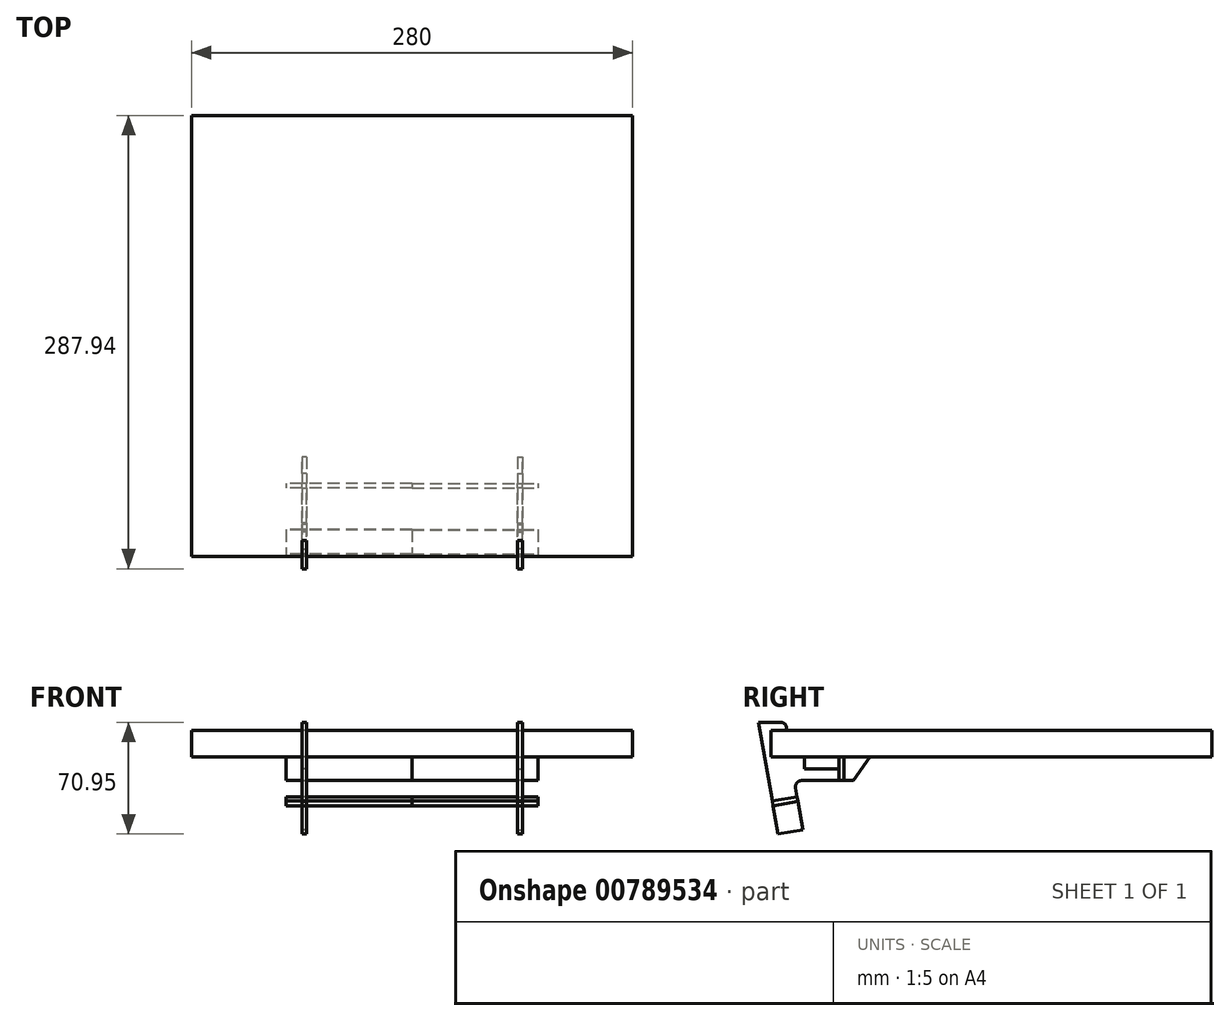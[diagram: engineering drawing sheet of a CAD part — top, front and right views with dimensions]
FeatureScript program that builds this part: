
annotation { "Feature Type Name" : "Feature", "Feature Type Description" : "" }
export const myFeature = defineFeature(function(context is Context, id is Id, definition is map)
    precondition{}
    {
        {
            var Q0;
            Q0=qCreatedBy(makeId("Top.planeOp"),FACE);
            var sketch = newSketch(context, id + "F0", { "sketchPlane" : qUnion([Q0])});
            skLineSegment(sketch, "E0.bottom", {"start": v(140, -85) * mm, "end": v(-140, -85) * mm});
            skLineSegment(sketch, "E0.top", {"start": v(140, 85) * mm, "end": v(-140, 85) * mm});
            skLineSegment(sketch, "E0.left", {"start": v(140, -85) * mm, "end": v(140, 85) * mm});
            skLineSegment(sketch, "E0.right", {"start": v(-140, -85) * mm, "end": v(-140, 85) * mm});
            skPoint(sketch, "E0.middle", {"position": v(0, 0) * mm});
            skSolve(sketch);
        }
        {
            var Q0;
            Q0=makeQuery(id+"F0.imprint","IMPRINT",FACE,{"disambiguationData":[TD([[makeQuery(id+"F0.imprint","IMPRINT",EDGE,{"derivedFrom":sQuery(id+"F0.wireOp",EDGE,"E0.bottom")}),-1.0]])]});
            extrude(context, id + "F1", {"entities" : qUnion([Q0]), "depth" : 17 * mm, "offsetDistance" : 25 * mm});
        }
        {
            var Q0;
            Q0=makeQuery(id+"F1.opExtrude","CAP_EDGE",EDGE,{"disambiguationData":[OSD([sQuery(id+"F0.wireOp",EDGE,"E0.bottom")])],"isStart":true});
            var Q1;
            Q1=qCreatedBy(makeId("Front.planeOp"),FACE);
            cPlane(context, id + "F2", {"entities" : qUnion([Q0, Q1]), "cplaneType" : CPlaneType.LINE_ANGLE, "offset" : 25 * mm, "angle" : 10 * degree, "oppositeDirection" : true, "width" : 150 * mm, "height" : 150 * mm});
        }
        {
            var Q0;
            Q0=qCreatedBy(id+"F2.planeOp",FACE);
            var sketch = newSketch(context, id + "F3", { "sketchPlane" : qUnion([Q0])});
            skLineSegment(sketch, "E1.bottom", {"start": v(70, 87.7) * mm, "end": v(67, 87.7) * mm});
            skLineSegment(sketch, "E1.top", {"start": v(70, -112.3) * mm, "end": v(67, -112.3) * mm});
            skLineSegment(sketch, "E1.left", {"start": v(70, 87.7) * mm, "end": v(70, -112.3) * mm});
            skLineSegment(sketch, "E1.right", {"start": v(67, 87.7) * mm, "end": v(67, -112.3) * mm});
            skSolve(sketch);
        }
        {
            var Q0;
            Q0=qSketchRegion(id+"F3",true);
            extrude(context, id + "F4", {"entities" : qUnion([Q0]), "oppositeDirection" : true, "depth" : 8 * mm, "offsetDistance" : 25 * mm, "hasSecondDirection" : true, "secondDirectionOppositeDirection" : false, "secondDirectionDepth" : 130 * mm});
        }
        {
            var Q0;
            Q0=makeQuery(id+"F1.opExtrude","SWEPT_BODY",BODY,{"disambiguationData":[OSD([sQuery(id+"F0.wireOp",EDGE,"E0.bottom"),sQuery(id+"F0.wireOp",EDGE,"E0.top"),sQuery(id+"F0.wireOp",EDGE,"E0.left"),sQuery(id+"F0.wireOp",EDGE,"E0.right")])]});
            var Q1;
            Q1=makeQuery(id+"F4.opExtrude","SWEPT_BODY",BODY,{"disambiguationData":[OSD([sQuery(id+"F3.wireOp",EDGE,"E1.bottom"),sQuery(id+"F3.wireOp",EDGE,"E1.top"),sQuery(id+"F3.wireOp",EDGE,"E1.left"),sQuery(id+"F3.wireOp",EDGE,"E1.right")])]});
            booleanBodies(context, id + "F5", {"operationType" : BooleanOperationType.SUBTRACTION, "tools" : qUnion([Q0]), "targets" : qUnion([Q1])});
        }
        {
            var Q0;
            Q0=makeQuery(id+"F4.opExtrude","SWEPT_FACE",FACE,{"disambiguationData":[OSD([sQuery(id+"F3.wireOp",EDGE,"E1.left")])]});
            var sketch = newSketch(context, id + "F6", { "sketchPlane" : qUnion([Q0])});
            skLineSegment(sketch, "E2.0", {"start": v(-31.06, 22) * mm, "end": v(164.2, 22) * mm});
            skLineSegment(sketch, "E3", {"start": v(62.6, -57.92) * mm, "end": v(22.04, 0) * mm});
            skLineSegment(sketch, "E4", {"start": v(22.04, 0) * mm, "end": v(90.98, -12.16) * mm, "construction": true});
            skLineSegment(sketch, "E5", {"start": v(75, 22) * mm, "end": v(75, 17) * mm});
            skLineSegment(sketch, "E6", {"start": v(84.37, -49.64) * mm, "end": v(64.67, -46.17) * mm});
            skLineSegment(sketch, "E7", {"start": v(62.6, -57.92) * mm, "end": v(64.67, -46.17) * mm});
            skPoint(sketch, "E8", {"position": v(97, 22) * mm});
            skPoint(sketch, "E9", {"position": v(19, 0) * mm});
            skSolve(sketch);
        }
        {
            var Q0;
            {var subQ0=sQuery(id+"F3.wireOp",EDGE,"E1.left");var subQ2=sQuery(id+"F3.wireOp",EDGE,"E1.bottom");var subQ3=makeQuery(id+"F4.opExtrude","SWEPT_EDGE",EDGE,{"disambiguationData":[OSD([subQ2,subQ0])]});Q0=makeQuery(id+"F6.imprint","IMPRINT",FACE,{"disambiguationData":[TD([[makeQuery(id+"F6.imprint","IMPRINT",EDGE,{"derivedFrom":subQ3}),1.0]])]});}
            var Q1;
            {var subQ0=sQuery(id+"F6.wireOp",EDGE,"E5");Q1=makeQuery(id+"F6.imprint","IMPRINT",FACE,{"disambiguationData":[TD([[makeQuery(id+"F6.imprint","IMPRINT",EDGE,{"derivedFrom":subQ0}),-1.0]])]});}
            var Q2;
            {var subQ2=sQuery(id+"F3.wireOp",EDGE,"E1.left");var subQ3=sQuery(id+"F3.wireOp",EDGE,"E1.top");var subQ8=makeQuery(id+"F4.opExtrude","SWEPT_EDGE",EDGE,{"disambiguationData":[OSD([subQ3,subQ2])]});Q2=makeQuery(id+"F6.imprint","IMPRINT",FACE,{"disambiguationData":[TD([[makeQuery(id+"F6.imprint","IMPRINT",EDGE,{"derivedFrom":subQ8}),-1.0]])]});}
            extrude(context, id + "F7", {"entities" : qUnion([Q0, Q1, Q2]), "operationType" : NewBodyOperationType.REMOVE, "oppositeDirection" : true, "depth" : 25 * mm, "offsetDistance" : 25 * mm});
        }
        {
            var Q0;
            Q0=makeQuery(id+"F4.opExtrude","SWEPT_FACE",FACE,{"disambiguationData":[OSD([sQuery(id+"F3.wireOp",EDGE,"E1.left")])]});
            var sketch = newSketch(context, id + "F8", { "sketchPlane" : qUnion([Q0])});
            skLineSegment(sketch, "E10.0", {"start": v(32.55, -15) * mm, "end": v(70.17, -15) * mm});
            skLineSegment(sketch, "E11.0", {"start": v(82.08, 52.55) * mm, "end": v(56.38, -93.2) * mm});
            skLineSegment(sketch, "E12.0", {"start": v(62.6, -57.92) * mm, "end": v(22.04, 0) * mm});
            skSolve(sketch);
        }
        {
            var Q0;
            {var subQ0=sQuery(id+"F8.wireOp",EDGE,"E10.0");Q0=makeQuery(id+"F8.imprint","IMPRINT",FACE,{"disambiguationData":[TD([[makeQuery(id+"F8.imprint","IMPRINT",EDGE,{"derivedFrom":subQ0}),-1.0]])]});}
            var Q1;
            Q1=makeQuery(id+"F4.opExtrude","SWEPT_FACE",FACE,{"disambiguationData":[OSD([sQuery(id+"F3.wireOp",EDGE,"E1.right")])]});
            extrude(context, id + "F9", {"entities" : qUnion([Q0]), "operationType" : NewBodyOperationType.REMOVE, "endBound" : BoundingType.UP_TO_SURFACE, "oppositeDirection" : true, "depth" : 25 * mm, "endBoundEntityFace" : qUnion([Q1]), "offsetDistance" : 25 * mm});
        }
        {
            var Q0;
            Q0=makeQuery(id+"F4.opExtrude","SWEPT_FACE",FACE,{"disambiguationData":[OSD([sQuery(id+"F3.wireOp",EDGE,"E1.right")])]});
            var sketch = newSketch(context, id + "F10", { "sketchPlane" : qUnion([Q0])});
            skLineSegment(sketch, "E13", {"start": v(-80.3, -49.64) * mm, "end": v(-97.67, 48.84) * mm});
            skLineSegment(sketch, "E14", {"start": v(-97.67, 48.84) * mm, "end": v(-105.31, 47.49) * mm});
            skLineSegment(sketch, "E15", {"start": v(-105.31, 47.49) * mm, "end": v(-116.05, -55.95) * mm});
            skLineSegment(sketch, "E16", {"start": v(-116.05, -55.95) * mm, "end": v(-80.3, -49.64) * mm});
            skSolve(sketch);
        }
        {
            var Q0;
            {var subQ1=sQuery(id+"F3.wireOp",EDGE,"E1.right");var subQ7=makeQuery(id+"F4.opExtrude","CAP_EDGE",EDGE,{"disambiguationData":[OSD([subQ1])],"isStart":false});Q0=makeQuery(id+"F10.imprint","IMPRINT",FACE,{"disambiguationData":[TD([[makeQuery(id+"F10.imprint","IMPRINT",EDGE,{"derivedFrom":subQ7}),1.0]])]});}
            extrude(context, id + "F11", {"entities" : qUnion([Q0]), "operationType" : NewBodyOperationType.REMOVE, "oppositeDirection" : true, "depth" : 25 * mm, "offsetDistance" : 25 * mm});
        }
        {
            var Q0;
            Q0=makeQuery(id+"F7.boolean.opBoolean","COPY",EDGE,{"derivedFrom":makeQuery(id+"F7.opExtrude","SWEPT_EDGE",EDGE,{"disambiguationData":[OSD([sQuery(id+"F6.wireOp",EDGE,"E2.0"),sQuery(id+"F6.wireOp",EDGE,"E5")])]})});
            var Q1;
            Q1=makeQuery(id+"F11.boolean.opBoolean","COPY",EDGE,{"derivedFrom":makeQuery(id+"F11.opExtrude","SWEPT_EDGE",EDGE,{"disambiguationData":[OSD([sQuery(id+"F3.wireOp",EDGE,"E1.right"),sQuery(id+"F6.wireOp",EDGE,"E2.0"),sQuery(id+"F10.wireOp",EDGE,"E13")])]})});
            var Q2;
            Q2=makeQuery(id+"F11.boolean.opBoolean","COPY",EDGE,{"derivedFrom":makeQuery(id+"F11.opExtrude","SWEPT_EDGE",EDGE,{"disambiguationData":[OSD([sQuery(id+"F3.wireOp",EDGE,"E1.right"),sQuery(id+"F6.wireOp",EDGE,"E6"),sQuery(id+"F10.wireOp",EDGE,"E13")])]})});
            var Q3;
            Q3=makeQuery(id+"F7.boolean.opBoolean","COPY",EDGE,{"derivedFrom":makeQuery(id+"F7.opExtrude","SWEPT_EDGE",EDGE,{"disambiguationData":[OSD([sQuery(id+"F6.wireOp",EDGE,"E6"),sQuery(id+"F6.wireOp",EDGE,"E7")])]})});
            var Q4;
            Q4=makeQuery(id+"F9.boolean.opBoolean","COPY",EDGE,{"derivedFrom":makeQuery(id+"F9.opExtrude","SWEPT_EDGE",EDGE,{"disambiguationData":[OSD([sQuery(id+"F8.wireOp",EDGE,"E10.0"),sQuery(id+"F8.wireOp",EDGE,"E11.0")])]})});
            var Q5;
            Q5=makeQuery(id+"F9.boolean.opBoolean","COPY",EDGE,{"derivedFrom":makeQuery(id+"F9.opExtrude","SWEPT_EDGE",EDGE,{"disambiguationData":[OSD([sQuery(id+"F8.wireOp",EDGE,"E10.0"),sQuery(id+"F8.wireOp",EDGE,"E12.0")])]})});
            var Q6;
            Q6=makeQuery(id+"F7.boolean.opBoolean","COPY",EDGE,{"derivedFrom":makeQuery(id+"F7.opExtrude","SWEPT_EDGE",EDGE,{"disambiguationData":[OSD([sQuery(id+"F0.wireOp",EDGE,"E0.bottom"),sQuery(id+"F0.wireOp",EDGE,"E0.top"),sQuery(id+"F0.wireOp",EDGE,"E0.left"),sQuery(id+"F0.wireOp",EDGE,"E0.right"),sQuery(id+"F3.wireOp",EDGE,"E1.left"),sQuery(id+"F6.wireOp",EDGE,"E3")])]})});
            fillet(context, id + "F12", {"entities" : qUnion([Q0, Q1, Q2, Q3, Q4, Q5, Q6]), "radius" : 4 * mm, "tangentPropagation" : true, "defaultsChanged" : false, "vertexSettings" : [], "allowEdgeOverflow" : false});
        }
        {
            var Q0;
            Q0=makeQuery(id+"F4.opExtrude","SWEPT_FACE",FACE,{"disambiguationData":[OSD([sQuery(id+"F3.wireOp",EDGE,"E1.right")])]});
            var sketch = newSketch(context, id + "F13", { "sketchPlane" : qUnion([Q0])});
            skLineSegment(sketch, "E17.bottom", {"start": v(-84.11, -28.06) * mm, "end": v(-83.6, -31.01) * mm});
            skLineSegment(sketch, "E17.top", {"start": v(-68.36, -25.28) * mm, "end": v(-67.84, -28.23) * mm});
            skLineSegment(sketch, "E17.left", {"start": v(-68.36, -25.28) * mm, "end": v(-84.11, -28.06) * mm});
            skLineSegment(sketch, "E17.right", {"start": v(-67.84, -28.23) * mm, "end": v(-83.6, -31.01) * mm});
            skLineSegment(sketch, "E18.bottom", {"start": v(-38.73, 0) * mm, "end": v(-41.73, 0) * mm});
            skLineSegment(sketch, "E18.top", {"start": v(-38.73, -15) * mm, "end": v(-41.73, -15) * mm});
            skLineSegment(sketch, "E18.left", {"start": v(-38.73, 0) * mm, "end": v(-38.73, -15) * mm});
            skLineSegment(sketch, "E18.right", {"start": v(-41.73, 0) * mm, "end": v(-41.73, -15) * mm});
            skLineSegment(sketch, "E19.0", {"start": v(-29.73, 0) * mm, "end": v(-85, 0) * mm});
            skLineSegment(sketch, "E20.0", {"start": v(-34.63, -15) * mm, "end": v(-65.4, -15) * mm});
            skLineSegment(sketch, "E21.0", {"start": v(-69.34, -19.7) * mm, "end": v(-65.37, -42.23) * mm});
            skLineSegment(sketch, "E22.0", {"start": v(-81.13, -45.01) * mm, "end": v(-92.11, 17.3) * mm});
            skSolve(sketch);
        }
        {
            var Q0;
            Q0=qSketchRegion(id+"F13",true);
            var Q1;
            Q1=qCreatedBy(makeId("Right.planeOp"),FACE);
            var Q2;
            Q2=makeQuery(id+"F4.opExtrude","SWEPT_FACE",FACE,{"disambiguationData":[OSD([sQuery(id+"F3.wireOp",EDGE,"E1.left")])]});
            extrude(context, id + "F14", {"entities" : qUnion([Q0]), "endBound" : BoundingType.UP_TO_SURFACE, "depth" : 25 * mm, "endBoundEntityFace" : qUnion([Q1]), "offsetDistance" : 25 * mm, "hasSecondDirection" : true, "secondDirectionBound" : BoundingType.UP_TO_SURFACE, "secondDirectionOppositeDirection" : true, "secondDirectionDepth" : 17.8 * mm, "secondDirectionBoundEntityFace" : qUnion([Q2]), "hasSecondDirectionOffset" : true, "secondDirectionOffsetDistance" : 10 * mm, "secondDirectionOffsetOppositeDirection" : true});
        }
        {
            var Q0;
            Q0=makeQuery(id+"F14.opExtrude","SWEPT_FACE",FACE,{"disambiguationData":[OSD([sQuery(id+"F13.wireOp",EDGE,"E18.left")])]});
            var sketch = newSketch(context, id + "F15", { "sketchPlane" : qUnion([Q0])});
            skLineSegment(sketch, "E23", {"start": v(67, 0) * mm, "end": v(67, -15) * mm});
            skLineSegment(sketch, "E24", {"start": v(70, 0) * mm, "end": v(70, -15) * mm});
            skLineSegment(sketch, "E25", {"start": v(67, -7.5) * mm, "end": v(70, -7.5) * mm});
            skLineSegment(sketch, "E26", {"start": v(67, 0) * mm, "end": v(70, 0) * mm});
            skLineSegment(sketch, "E27", {"start": v(70, -15) * mm, "end": v(67, -15) * mm});
            skSolve(sketch);
        }
        {
            var Q0;
            {var subQ3=sQuery(id+"F15.wireOp",EDGE,"E25");Q0=makeQuery(id+"F15.imprint","IMPRINT",FACE,{"disambiguationData":[TD([[makeQuery(id+"F15.imprint","IMPRINT",EDGE,{"derivedFrom":subQ3}),1.0]])]});}
            extrude(context, id + "F16", {"entities" : qUnion([Q0]), "operationType" : NewBodyOperationType.REMOVE, "oppositeDirection" : true, "depth" : 25 * mm, "offsetDistance" : 25 * mm});
        }
        {
            var Q0;
            {var subQ3=sQuery(id+"F15.wireOp",EDGE,"E25");Q0=makeQuery(id+"F15.imprint","IMPRINT",FACE,{"disambiguationData":[TD([[makeQuery(id+"F15.imprint","IMPRINT",EDGE,{"derivedFrom":subQ3}),-1.0]])]});}
            var Q1;
            Q1=makeQuery(id+"F14.opExtrude","SWEPT_FACE",FACE,{"disambiguationData":[OSD([sQuery(id+"F13.wireOp",EDGE,"E18.right")])]});
            extrude(context, id + "F17", {"entities" : qUnion([Q0]), "operationType" : NewBodyOperationType.REMOVE, "endBound" : BoundingType.UP_TO_SURFACE, "oppositeDirection" : true, "depth" : 25 * mm, "endBoundEntityFace" : qUnion([Q1]), "offsetDistance" : 25 * mm});
        }
        {
            var Q0;
            Q0=makeQuery(id+"F14.opExtrude","SWEPT_FACE",FACE,{"disambiguationData":[OSD([sQuery(id+"F13.wireOp",EDGE,"E17.left")])]});
            var sketch = newSketch(context, id + "F18", { "sketchPlane" : qUnion([Q0])});
            skLineSegment(sketch, "E28", {"start": v(-67, -87.7) * mm, "end": v(-67, -71.7) * mm});
            skLineSegment(sketch, "E29", {"start": v(-70, -87.7) * mm, "end": v(-70, -71.7) * mm});
            skLineSegment(sketch, "E30", {"start": v(-67, -79.7) * mm, "end": v(-70, -79.7) * mm});
            skLineSegment(sketch, "E31", {"start": v(-67, -79.7) * mm, "end": v(-67, -87.7) * mm});
            skLineSegment(sketch, "E32", {"start": v(-67, -87.7) * mm, "end": v(-70, -87.7) * mm});
            skLineSegment(sketch, "E33", {"start": v(-70, -71.7) * mm, "end": v(-67, -71.7) * mm});
            skLineSegment(sketch, "E34", {"start": v(-67, -90.82) * mm, "end": v(-67, -67.87) * mm});
            skLineSegment(sketch, "E35.0", {"start": v(-70, -87.7) * mm, "end": v(-67, -87.7) * mm});
            skLineSegment(sketch, "E36.0", {"start": v(-67, -71.7) * mm, "end": v(-70, -71.7) * mm});
            skSolve(sketch);
        }
        {
            var Q0;
            {var subQ2=sQuery(id+"F18.wireOp",EDGE,"E30");Q0=makeQuery(id+"F18.imprint","IMPRINT",FACE,{"disambiguationData":[TD([[makeQuery(id+"F18.imprint","IMPRINT",EDGE,{"derivedFrom":subQ2}),1.0]])]});}
            var Q1;
            Q1=makeQuery(id+"F14.opExtrude","SWEPT_FACE",FACE,{"disambiguationData":[OSD([sQuery(id+"F13.wireOp",EDGE,"E17.right")])]});
            extrude(context, id + "F19", {"entities" : qUnion([Q0]), "operationType" : NewBodyOperationType.REMOVE, "endBound" : BoundingType.UP_TO_SURFACE, "oppositeDirection" : true, "depth" : 25 * mm, "endBoundEntityFace" : qUnion([Q1]), "offsetDistance" : 25 * mm});
        }
        {
            var Q0;
            {var subQ3=sQuery(id+"F18.wireOp",EDGE,"E30");Q0=makeQuery(id+"F18.imprint","IMPRINT",FACE,{"disambiguationData":[TD([[makeQuery(id+"F18.imprint","IMPRINT",EDGE,{"derivedFrom":subQ3}),-1.0]])]});}
            var Q1;
            Q1=makeQuery(id+"F14.opExtrude","SWEPT_FACE",FACE,{"disambiguationData":[OSD([sQuery(id+"F13.wireOp",EDGE,"E17.right")])]});
            extrude(context, id + "F20", {"entities" : qUnion([Q0]), "operationType" : NewBodyOperationType.REMOVE, "endBound" : BoundingType.UP_TO_SURFACE, "oppositeDirection" : true, "depth" : 25 * mm, "endBoundEntityFace" : qUnion([Q1]), "offsetDistance" : 25 * mm});
        }
        {
            var Q0;
            Q0=makeQuery(id+"F4.opExtrude","SWEPT_BODY",BODY,{"disambiguationData":[OSD([sQuery(id+"F3.wireOp",EDGE,"E1.bottom"),sQuery(id+"F3.wireOp",EDGE,"E1.top"),sQuery(id+"F3.wireOp",EDGE,"E1.left"),sQuery(id+"F3.wireOp",EDGE,"E1.right")])]});
            var Q1;
            Q1=qCreatedBy(makeId("Right.planeOp"),FACE);
            mirror(context, id + "F21", {"entities" : qUnion([Q0]), "mirrorPlane" : qUnion([Q1])});
        }
        {
            var Q0;
            Q0=makeQuery(id+"F14.opExtrude","SWEPT_BODY",BODY,{"disambiguationData":[OSD([sQuery(id+"F13.wireOp",EDGE,"E18.bottom"),sQuery(id+"F13.wireOp",EDGE,"E18.top"),sQuery(id+"F13.wireOp",EDGE,"E18.left"),sQuery(id+"F13.wireOp",EDGE,"E18.right")])]});
            var Q1;
            Q1=makeQuery(id+"F14.opExtrude","SWEPT_BODY",BODY,{"disambiguationData":[OSD([sQuery(id+"F13.wireOp",EDGE,"E17.bottom"),sQuery(id+"F13.wireOp",EDGE,"E17.top"),sQuery(id+"F13.wireOp",EDGE,"E17.left"),sQuery(id+"F13.wireOp",EDGE,"E17.right")])]});
            var Q2;
            Q2=qCreatedBy(makeId("Right.planeOp"),FACE);
            mirror(context, id + "F22", {"operationType" : NewBodyOperationType.ADD, "entities" : qUnion([Q0, Q1]), "mirrorPlane" : qUnion([Q2])});
        }
        {
            var Q0;
            {var subQ0=makeQuery(id+"F14.opExtrude","SWEPT_FACE",FACE,{"disambiguationData":[OSD([sQuery(id+"F13.wireOp",EDGE,"E17.right")])]});Q0=makeQuery(id+"F22.boolean.opBoolean","MERGE",FACE,{"derivedFrom":[subQ0,makeQuery(id+"F22.opPattern","COPY",FACE,{"derivedFrom":subQ0,"instanceName":"1"})]});}
            var sketch = newSketch(context, id + "F23", { "sketchPlane" : qUnion([Q0])});
            skLineSegment(sketch, "E37.0.0", {"start": v(67, 87.87) * mm, "end": v(-67, 87.87) * mm});
            skLineSegment(sketch, "E37.0.1", {"start": v(-67, 87.87) * mm, "end": v(-67, 79.7) * mm});
            skLineSegment(sketch, "E37.0.2", {"start": v(-67, 79.7) * mm, "end": v(-70, 79.7) * mm});
            skLineSegment(sketch, "E37.0.3", {"start": v(-70, 79.7) * mm, "end": v(-70, 79.7) * mm});
            skLineSegment(sketch, "E37.0.4", {"start": v(-70, 79.7) * mm, "end": v(-80, 79.7) * mm});
            skLineSegment(sketch, "E37.0.5", {"start": v(-80, 79.7) * mm, "end": v(-80, 71.7) * mm});
            skLineSegment(sketch, "E37.0.6", {"start": v(-80, 71.7) * mm, "end": v(80, 71.7) * mm});
            skLineSegment(sketch, "E37.0.7", {"start": v(80, 71.7) * mm, "end": v(80, 71.7) * mm});
            skLineSegment(sketch, "E37.0.8", {"start": v(80, 71.7) * mm, "end": v(70, 71.7) * mm});
            skLineSegment(sketch, "E37.0.9", {"start": v(70, 79.7) * mm, "end": v(70, 71.7) * mm});
            skLineSegment(sketch, "E37.0.10", {"start": v(70, 79.7) * mm, "end": v(67, 79.7) * mm});
            skLineSegment(sketch, "E37.0.11", {"start": v(67, 79.7) * mm, "end": v(67, 87.87) * mm});
            skSolve(sketch);
        }
        {
            var Q0;
            Q0=qCreatedBy(makeId("Top.planeOp"),FACE);
            var sketch = newSketch(context, id + "F24", { "sketchPlane" : qUnion([Q0])});
            skLineSegment(sketch, "E38.bottom", {"start": v(140, -85) * mm, "end": v(-140, -85) * mm});
            skLineSegment(sketch, "E38.top", {"start": v(140, 195) * mm, "end": v(-140, 195) * mm});
            skLineSegment(sketch, "E38.left", {"start": v(140, -85) * mm, "end": v(140, 195) * mm});
            skLineSegment(sketch, "E38.right", {"start": v(-140, -85) * mm, "end": v(-140, 195) * mm});
            skPoint(sketch, "E38.middle", {"position": v(0, 55) * mm});
            skPoint(sketch, "E39.0", {"position": v(70, -85) * mm});
            skSolve(sketch);
        }
        {
            var Q0;
            Q0=makeQuery(id+"F24.imprint","IMPRINT",FACE,{"disambiguationData":[TD([[makeQuery(id+"F24.imprint","IMPRINT",EDGE,{"derivedFrom":sQuery(id+"F24.wireOp",EDGE,"E38.bottom")}),-1.0]])]});
            extrude(context, id + "F25", {"entities" : qUnion([Q0]), "depth" : 17 * mm, "offsetDistance" : 25 * mm});
        }
    });
